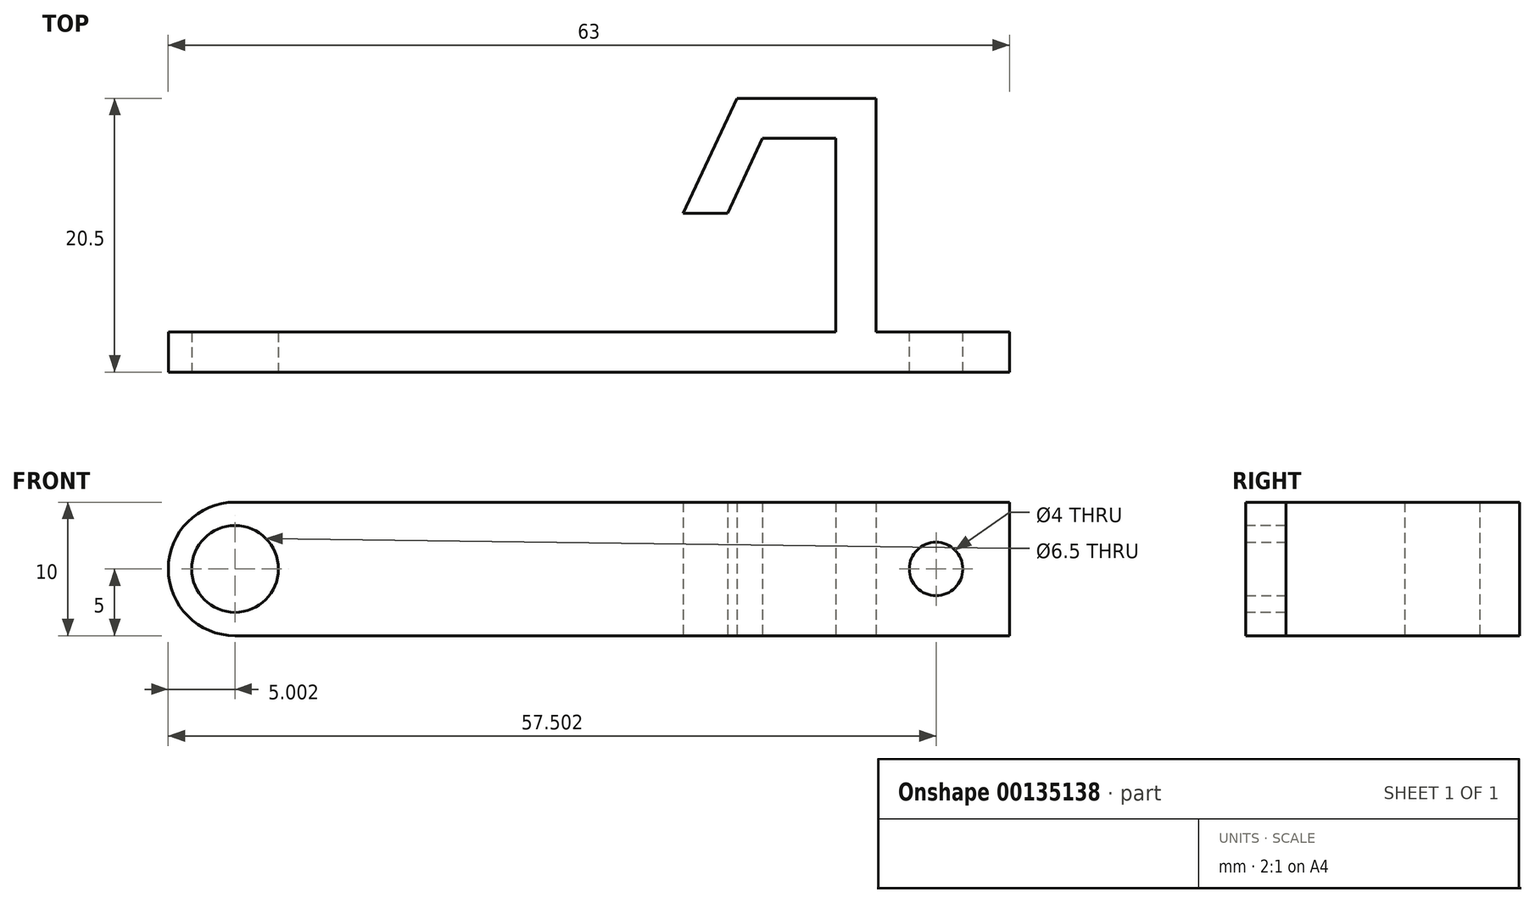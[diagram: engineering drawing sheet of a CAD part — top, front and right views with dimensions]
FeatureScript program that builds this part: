
annotation { "Feature Type Name" : "Feature", "Feature Type Description" : "" }
export const myFeature = defineFeature(function(context is Context, id is Id, definition is map)
    precondition{}
    {
        {
            var Q0;
            Q0=qCreatedBy(makeId("Top.planeOp"),FACE);
            var sketch = newSketch(context, id + "F0", { "sketchPlane" : qUnion([Q0])});
            skLineSegment(sketch, "E0", {"start": v(10.7, -11.9) * mm, "end": v(-2.3, -11.9) * mm});
            skLineSegment(sketch, "E1", {"start": v(-2.3, -11.9) * mm, "end": v(-2.3, 5.6) * mm});
            skLineSegment(sketch, "E2", {"start": v(-2.3, 5.6) * mm, "end": v(-7.8, 5.6) * mm});
            skLineSegment(sketch, "E3", {"start": v(-7.8, 5.6) * mm, "end": v(-10.41, 0) * mm});
            skLineSegment(sketch, "E4", {"start": v(-10.41, 0) * mm, "end": v(-13.72, 0) * mm});
            skLineSegment(sketch, "E5", {"start": v(-13.72, 0) * mm, "end": v(-9.7, 8.6) * mm});
            skLineSegment(sketch, "E6", {"start": v(-9.7, 8.6) * mm, "end": v(0.7, 8.6) * mm});
            skLineSegment(sketch, "E7", {"start": v(0.7, 8.6) * mm, "end": v(0.7, -8.9) * mm});
            skLineSegment(sketch, "E8", {"start": v(0.7, -8.9) * mm, "end": v(10.7, -8.9) * mm});
            skLineSegment(sketch, "E9", {"start": v(10.7, -8.9) * mm, "end": v(10.7, -11.9) * mm});
            skLineSegment(sketch, "E10.bottom", {"start": v(-2.3, -8.9) * mm, "end": v(-52.3, -8.9) * mm});
            skLineSegment(sketch, "E10.top", {"start": v(-2.3, -11.9) * mm, "end": v(-52.3, -11.9) * mm});
            skLineSegment(sketch, "E10.left", {"start": v(-2.3, -8.9) * mm, "end": v(-2.3, -11.9) * mm});
            skLineSegment(sketch, "E10.right", {"start": v(-52.3, -8.9) * mm, "end": v(-52.3, -11.9) * mm});
            skSolve(sketch);
        }
        {
            var Q0;
            Q0 = qSketchRegion(id + "F0", true);
            extrude(context, id + "F1", {"entities" : qUnion([Q0]), "depth" : 10 * mm, "offsetDistance" : 25 * mm});
        }
        {
            var Q0;
            Q0=makeQuery(id+"F1.opExtrude","SWEPT_FACE",FACE,{"disambiguationData":[OSD([sQuery(id+"F0.wireOp",EDGE,"E8")])]});
            var sketch = newSketch(context, id + "F2", { "sketchPlane" : qUnion([Q0])});
            skPoint(sketch, "E11", {"position": v(-5.2, 5) * mm});
            skSolve(sketch);
        }
        {
            var Q0;
            Q0=sQuery(id+"F2.wireOp",VERTEX,"E11");
            var Q1;
            Q1=makeQuery(id+"F1.opExtrude","SWEPT_BODY",BODY,{"disambiguationData":[OSD([sQuery(id+"F0.wireOp",EDGE,"E0"),sQuery(id+"F0.wireOp",EDGE,"E1"),sQuery(id+"F0.wireOp",EDGE,"E2"),sQuery(id+"F0.wireOp",EDGE,"E3"),sQuery(id+"F0.wireOp",EDGE,"E4"),sQuery(id+"F0.wireOp",EDGE,"E5"),sQuery(id+"F0.wireOp",EDGE,"E6"),sQuery(id+"F0.wireOp",EDGE,"E7"),sQuery(id+"F0.wireOp",EDGE,"E8"),sQuery(id+"F0.wireOp",EDGE,"E9")])]});
            hole(context, id + "F3", {"style" : HoleStyle.SIMPLE, "endStyle" : HoleEndStyle.THROUGH, "holeDiameter" : 4 * mm, "locations" : qUnion([Q0]), "scope" : qUnion([Q1]), "isTappedThrough" : true});
        }
        {
            var Q0;
            Q0=makeQuery(id+"F1.opExtrude","SWEPT_FACE",FACE,{"disambiguationData":[OSD([sQuery(id+"F0.wireOp",EDGE,"E0"),sQuery(id+"F0.wireOp",EDGE,"E10.top")])]});
            var sketch = newSketch(context, id + "F4", { "sketchPlane" : qUnion([Q0])});
            skPoint(sketch, "E12", {"position": v(-47.3, 5) * mm});
            skSolve(sketch);
        }
        {
            var Q0;
            Q0=makeQuery(id+"F1.opExtrude","CAP_EDGE",EDGE,{"disambiguationData":[OSD([sQuery(id+"F0.wireOp",EDGE,"E10.right")])],"isStart":false});
            var Q1;
            Q1=makeQuery(id+"F1.opExtrude","CAP_EDGE",EDGE,{"disambiguationData":[OSD([sQuery(id+"F0.wireOp",EDGE,"E10.right")])],"isStart":true});
            fillet(context, id + "F5", {"entities" : qUnion([Q0, Q1]), "radius" : 5 * mm, "tangentPropagation" : true, "allowEdgeOverflow" : false});
        }
        {
            var Q0;
            Q0=sQuery(id+"F4.wireOp",VERTEX,"E12");
            var Q1;
            Q1=makeQuery(id+"F1.opExtrude","SWEPT_BODY",BODY,{"disambiguationData":[OSD([sQuery(id+"F0.wireOp",EDGE,"E0"),sQuery(id+"F0.wireOp",EDGE,"E1"),sQuery(id+"F0.wireOp",EDGE,"E2"),sQuery(id+"F0.wireOp",EDGE,"E3"),sQuery(id+"F0.wireOp",EDGE,"E4"),sQuery(id+"F0.wireOp",EDGE,"E5"),sQuery(id+"F0.wireOp",EDGE,"E6"),sQuery(id+"F0.wireOp",EDGE,"E7"),sQuery(id+"F0.wireOp",EDGE,"E8"),sQuery(id+"F0.wireOp",EDGE,"E9"),sQuery(id+"F0.wireOp",EDGE,"E10.bottom"),sQuery(id+"F0.wireOp",EDGE,"E10.top"),sQuery(id+"F0.wireOp",EDGE,"E10.right")])]});
            hole(context, id + "F6", {"style" : HoleStyle.SIMPLE, "endStyle" : HoleEndStyle.THROUGH, "holeDiameter" : 6.5 * mm, "majorDiameter" : 5 * mm, "isTappedThrough" : true, "tappedDepth" : 12 * mm, "tapClearance" : 3, "startFromSketch" : true, "locations" : qUnion([Q0]), "scope" : qUnion([Q1])});
        }
    });
